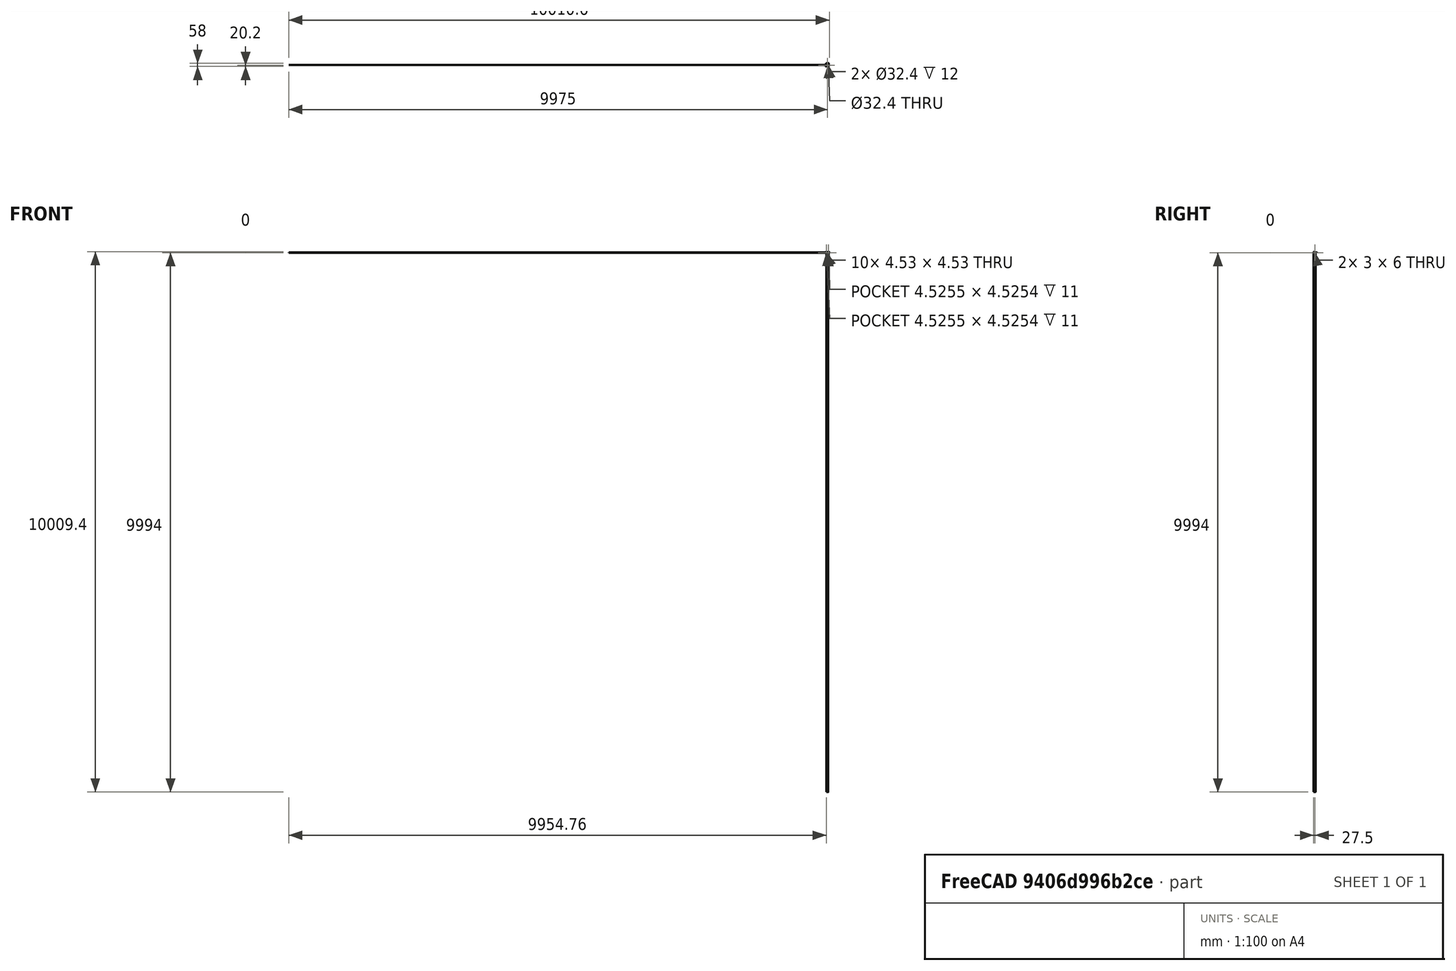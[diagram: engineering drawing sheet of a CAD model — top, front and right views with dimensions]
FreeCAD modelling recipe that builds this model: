
FCSTD DOCUMENT  (FreeCAD 0.16R)
Label: cargiblock2
License: All rights reserved
LicenseURL: http://en.wikipedia.org/wiki/All_rights_reserved
objects: Sketcher::SketchObject×8, PartDesign::Pocket×6, PartDesign::Fillet×3, PartDesign::Pad×2, PartDesign::Chamfer×1, Mesh::Feature×1
note: 28 computed .brp shape members not serialized (recipe doc carries the construction recipe); baked Part::Feature solids carry a one-line shape summary decoded from their .brp

FEATURE [Sketcher::SketchObject] Sketch
  sketch-geometry (4):
    g0: LineSegment StartX=-25 StartY=28 StartZ=0 EndX=25 EndY=28 EndZ=0
    g1: LineSegment StartX=25 StartY=28 StartZ=0 EndX=25 EndY=-28 EndZ=0
    g2: LineSegment StartX=25 StartY=-28 StartZ=0 EndX=-25 EndY=-28 EndZ=0
    g3: LineSegment StartX=-25 StartY=-28 StartZ=0 EndX=-25 EndY=28 EndZ=0
  constraints (11):
    c: Coincident(g0,g1)
    c: Coincident(g1,g2)
    c: Coincident(g2,g3)
    c: Coincident(g3,g0)
    c: Horizontal(g0)
    c: Horizontal(g2)
    c: Vertical(g1)
    c: Vertical(g3)
    c: Symmetric(g1,g0,g-1)
    c: Distance(g2) = 50
    c: Distance(g1) = 56
FEATURE [PartDesign::Pad] Pad
  Length = 12
  Length2 = 100
  Sketch = -> Sketch
  Type = 0
FEATURE [Sketcher::SketchObject] Sketch001
  ExternalGeometry = -> [Pad]
  Placement = pos=(0,0,12) rot=(0,0,1;0rad)
  Support = -> Pad [Face6]
  sketch-geometry (1):
    g0: Circle CenterX=0 CenterY=-7.8 CenterZ=0 NormalX=0 NormalY=0 NormalZ=1 Radius=16.2
  constraints (3):
    c: PointOnObject(g0,g-2)
    c: Radius(g0) = 16.2
    c: Distance(g0,g-3) = 20.2
FEATURE [PartDesign::Pocket] Pocket
  Length = 5
  Sketch = -> Sketch001
  Type = 1
FEATURE [Sketcher::SketchObject] Sketch009
  Placement = pos=(0,28,0) rot=(0,0.707107,0.707107;3.14159rad)
  Support = -> Pocket [Face1]
  sketch-geometry (4):
    g0: LineSegment StartX=25 StartY=12 StartZ=0 EndX=-34.4643 EndY=20 EndZ=0
    g1: LineSegment StartX=-34.4643 StartY=20 StartZ=0 EndX=-34.4643 EndY=0 EndZ=0
    g2: LineSegment StartX=-34.4643 StartY=0 StartZ=0 EndX=25 EndY=0 EndZ=0
    g3: LineSegment StartX=25 StartY=0 StartZ=0 EndX=25 EndY=12 EndZ=0
  constraints (7):
    c: Coincident(g0,g1)
    c: Vertical(g1)
    c: Coincident(g1,g2)
    c: Coincident(g2,g3)
    c: Coincident(g3,g0)
    c: Distance(g0) = 60
    c: Distance(g1) = 20
FEATURE [PartDesign::Pad] Pad001
  Length = 2
  Length2 = 100
  Sketch = -> Sketch009
  Type = 0
FEATURE [Sketcher::SketchObject] Sketch004
  Placement = pos=(0,0,12) rot=(0,0,1;0rad)
  Support = -> Pad001 [Face5]
  sketch-geometry (4):
    g0: LineSegment StartX=-36.7102 StartY=-6.29664 StartZ=0 EndX=35.607 EndY=-6.29664 EndZ=0
    g1: LineSegment StartX=35.607 StartY=-6.29664 StartZ=0 EndX=35.607 EndY=-8.29664 EndZ=0
    g2: LineSegment StartX=35.607 StartY=-8.29664 StartZ=0 EndX=-36.7102 EndY=-8.29664 EndZ=0
    g3: LineSegment StartX=-36.7102 StartY=-8.29664 StartZ=0 EndX=-36.7102 EndY=-6.29664 EndZ=0
  constraints (9):
    c: Coincident(g0,g1)
    c: Coincident(g1,g2)
    c: Coincident(g2,g3)
    c: Coincident(g3,g0)
    c: Horizontal(g0)
    c: Horizontal(g2)
    c: Vertical(g1)
    c: Vertical(g3)
    c: Distance(g1) = 2
FEATURE [PartDesign::Pocket] Pocket001
  Length = 11.9
  Sketch = -> Sketch004
  Type = 0
FEATURE [Sketcher::SketchObject] Sketch005
  Placement = pos=(0,-28,0) rot=(1,0,0;1.5708rad)
  Support = -> Pocket001 [Face1]
  sketch-geometry (8):
    g0: LineSegment StartX=-40.0409 StartY=13.5056 StartZ=0 EndX=-15 EndY=13.5056 EndZ=0
    g1: LineSegment StartX=-15 StartY=13.5056 StartZ=0 EndX=-15 EndY=-4.18064 EndZ=0
    g2: LineSegment StartX=-15 StartY=-4.18064 StartZ=0 EndX=-40.0409 EndY=-4.18064 EndZ=0
    g3: LineSegment StartX=-40.0409 StartY=-4.18064 StartZ=0 EndX=-40.0409 EndY=13.5056 EndZ=0
    g4: LineSegment StartX=15 StartY=21.4233 StartZ=0 EndX=27.2081 EndY=21.4233 EndZ=0
    g5: LineSegment StartX=27.2081 StartY=21.4233 StartZ=0 EndX=27.2081 EndY=-29.1676 EndZ=0
    g6: LineSegment StartX=27.2081 StartY=-29.1676 StartZ=0 EndX=15 EndY=-29.1676 EndZ=0
    g7: LineSegment StartX=15 StartY=-29.1676 StartZ=0 EndX=15 EndY=21.4233 EndZ=0
  constraints (16):
    c: Coincident(g0,g1)
    c: Coincident(g1,g2)
    c: Coincident(g2,g3)
    c: Coincident(g3,g0)
    c: Horizontal(g0)
    c: Horizontal(g2)
    c: Vertical(g1)
    c: Vertical(g3)
    c: Coincident(g4,g5)
    c: Coincident(g5,g6)
    c: Coincident(g6,g7)
    c: Coincident(g7,g4)
    c: Horizontal(g4)
    c: Horizontal(g6)
    c: Vertical(g5)
    c: Vertical(g7)
FEATURE [PartDesign::Pocket] Pocket002
  Length = 5
  Sketch = -> Sketch005
  Type = 0
FEATURE [Sketcher::SketchObject] Sketch003
  Placement = pos=(25,0,0) rot=(0.57735,0.57735,0.57735;2.0944rad)
  Support = -> Pocket002 [Face10]
  sketch-geometry (4):
    g0: LineSegment StartX=-2 StartY=9 StartZ=0 EndX=1 EndY=9 EndZ=0
    g1: LineSegment StartX=1 StartY=9 StartZ=0 EndX=1 EndY=3 EndZ=0
    g2: LineSegment StartX=1 StartY=3 StartZ=0 EndX=-2 EndY=3 EndZ=0
    g3: LineSegment StartX=-2 StartY=3 StartZ=0 EndX=-2 EndY=9 EndZ=0
  constraints (12):
    c: Coincident(g0,g1)
    c: Coincident(g1,g2)
    c: Coincident(g2,g3)
    c: Coincident(g3,g0)
    c: Horizontal(g0)
    c: Horizontal(g2)
    c: Vertical(g1)
    c: Vertical(g3)
    c: Distance(g3) = 6
    c: Distance(g2) = 3
    c: DistanceY(g-1,g1) = 3
    c: DistanceX(g-2,g0) = -2
FEATURE [PartDesign::Pocket] Pocket003
  Length = 5
  Sketch = -> Sketch003
  Type = 1
FEATURE [Sketcher::SketchObject] Sketch002
  Placement = pos=(0,-23,0) rot=(1,0,0;1.5708rad)
  Support = -> Pocket003 [Face8]
  sketch-geometry (8):
    g0: LineSegment StartX=-22.5 StartY=6 StartZ=0 EndX=-20.2373 EndY=8.26274 EndZ=0
    g1: LineSegment StartX=-20.2373 StartY=8.26274 StartZ=0 EndX=-17.9745 EndY=6 EndZ=0
    g2: LineSegment StartX=-17.9745 StartY=6 StartZ=0 EndX=-20.2373 EndY=3.73726 EndZ=0
    g3: LineSegment StartX=-20.2373 StartY=3.73726 StartZ=0 EndX=-22.5 EndY=6 EndZ=0
    g4: LineSegment StartX=17.9745 StartY=6 StartZ=0 EndX=20.2373 EndY=8.26274 EndZ=0
    g5: LineSegment StartX=20.2373 StartY=8.26274 StartZ=0 EndX=22.5 EndY=6 EndZ=0
    g6: LineSegment StartX=22.5 StartY=6 StartZ=0 EndX=20.2373 EndY=3.73726 EndZ=0
    g7: LineSegment StartX=20.2373 StartY=3.73726 StartZ=0 EndX=17.9745 EndY=6 EndZ=0
  constraints (20):
    c: Coincident(g0,g1)
    c: Coincident(g1,g2)
    c: Coincident(g2,g3)
    c: Coincident(g3,g0)
    c: Coincident(g4,g5)
    c: Coincident(g5,g6)
    c: Coincident(g6,g7)
    c: Coincident(g7,g4)
    c: Equal(g5,g6)
    c: Equal(g6,g2)
    c: Equal(g2,g3)
    c: Distance(g5) = 3.2
    c: Perpendicular(g1,g2)
    c: Perpendicular(g5,g6)
    c: Perpendicular(g4,g7)
    c: Perpendicular(g0,g3)
    c: Equal(g7,g5)
    c: Equal(g0,g2)
    c: Angle(g4) = 0.785398
    c: Angle(g0) = 0.785398
FEATURE [PartDesign::Pocket] Pocket004
  Length = 35
  Sketch = -> Sketch002
  Type = 0
FEATURE [PartDesign::Fillet] Fillet
  Base = -> Pocket004 [Edge4,Edge23,Edge42,Edge2,Edge13,Edge28]
  Radius = 1.8
FEATURE [Sketcher::SketchObject] Sketch010
  Placement = pos=(0,0,0) rot=(1,0,0;3.14159rad)
  Support = -> Fillet [Face2]
  sketch-geometry (3):
    g0: ArcOfCircle CenterX=22.3007 CenterY=35.0589 CenterZ=0 NormalX=0 NormalY=0 NormalZ=1 Radius=71.5282 StartAngle=3.77489 EndAngle=4.59259
    g1: LineSegment StartX=13.7519 StartY=-35.9566 StartZ=0 EndX=-64.8306 EndY=-41.4878 EndZ=0
    g2: LineSegment StartX=-64.8306 StartY=-41.4878 StartZ=0 EndX=-35.3566 EndY=-7.27204 EndZ=0
  constraints (3):
    c: Coincident(g0,g1)
    c: Coincident(g1,g2)
    c: Coincident(g2,g0)
FEATURE [PartDesign::Pocket] Pocket005
  Length = 5
  Sketch = -> Sketch010
  Type = 1
FEATURE [PartDesign::Chamfer] Chamfer
  Base = -> Pocket005 [Edge65]
  Size = 3
FEATURE [PartDesign::Fillet] Fillet001
  Base = -> Chamfer [Edge45]
  Radius = 5
FEATURE [PartDesign::Fillet] Fillet002
  Base = -> Fillet001 [Edge10]
  Radius = 5
FEATURE [Mesh::Feature] Mesh  label="Fillet002 (Meshed)"
